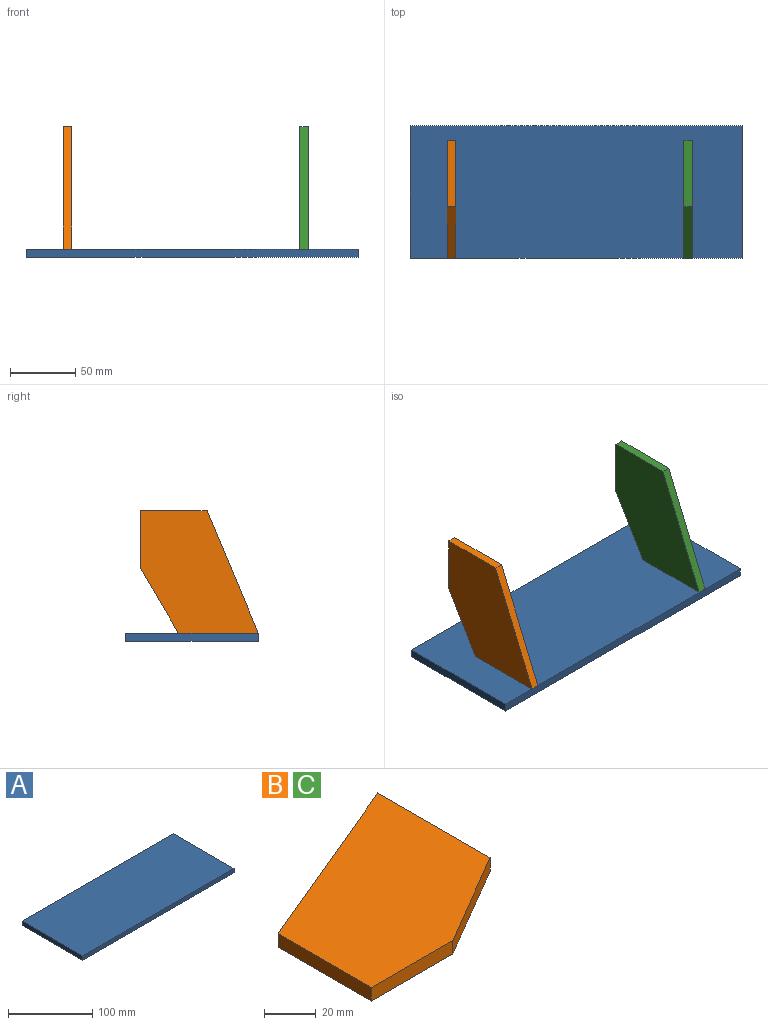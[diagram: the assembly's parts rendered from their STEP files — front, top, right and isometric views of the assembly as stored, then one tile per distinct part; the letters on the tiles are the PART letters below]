
ASSEMBLY  parts=3 mates=2
PART A: 6 faces, bbox 254x101.6x6.4 mm
  f0: plane 101.6x6.35mm, normal (-1,0,0), area 645.2mm2, adj f1,f3,f4,f5
  f1: plane 254x6.35mm, normal (0,-1,0), area 1612.9mm2, adj f0,f2,f4,f5
  f2: plane 101.6x6.35mm, normal (1,0,0), area 645.2mm2, adj f1,f3,f4,f5
  f3: plane 254x6.35mm, normal (0,1,0), area 1612.9mm2, adj f0,f2,f4,f5
  f4: plane 254x101.6mm, normal (0,0,1), area 25806.4mm2, adj f0,f1,f2,f3
  f5: plane 254x101.6mm, normal (0,0,-1), area 25806.4mm2, adj f0,f1,f2,f3
PART B: 7 faces, bbox 93.7x90.1x6.4 mm
  f0: plane 93.7x39.29mm, normal (-0.39,0.92,0), area 645.2mm2, adj f1,f4,f5,f6
  f1: plane 50.8x6.35mm, normal (-1,0,0), area 322.6mm2, adj f0,f2,f5,f6
  f2: plane 44.45x6.35mm, normal (0,-1,0), area 282.3mm2, adj f1,f3,f5,f6
  f3: plane 49.25x29mm, normal (0.51,-0.86,0), area 362.9mm2, adj f2,f4,f5,f6
  f4: plane 61.09x6.35mm, normal (1,0,0), area 387.9mm2, adj f0,f3,f5,f6
  f5: plane 93.7x90.09mm, normal (0,0,1), area 5886.3mm2, adj f0,f1,f2,f3,f4
  f6: plane 93.7x90.09mm, normal (0,0,-1), area 5886.3mm2, adj f0,f1,f2,f3,f4
PART C: same geometry as B
PLACE A t=(-3.26,27.7,7.41)mm
PLACE B rot(axis=(0.71,0,-0.71),180deg) t=(31.67,117.8,107.46)mm
PLACE C rot(axis=(0.71,0,-0.71),180deg) t=(212.64,117.8,107.46)mm
MATE fastened B.f4 <-> A.f4  axis (0,0,-1) through (28.49,58.25,13.76)mm
MATE fastened C.f4 <-> A.f4  axis (0,0,-1) through (209.47,58.25,13.76)mm
